# Revit family: Domotics-DomesticRanges-GEWISS-27COMBI_SYSTEM-IP55_4P+4P
name_source: partatom
category: Apparecchi elettrici
revit_build: Autodesk Revit 2016 (Build: 20161004_0715(x64)
units: mm (PartAtom-declared; Revit-internal decimal feet)

## family parameters
Condiviso = No
Host = Superficie
Mantenere orientamento annotazione = No
Numero OmniClass = 23.80.30.14.24
Punto di calcolo locali = No
Quota connettore circolare = Usa diametro
Taglio con vuoti quando caricato = Sì
Tipo di parte = Normale
Titolo OmniClass = Junction Boxes

## types (1)
- Domotics-DomesticRanges-GEWISS-27COMBI_SYSTEM-IP55_4P+4P
    Catalogue = DOMOTICS
    Catalogue Range = 27COMBI
    Colour = Grey RAL 7035
    Compartment pre-arrangement = 2
    Configuration = Module 4 x 2
    Description: = 8 gang
    Descrizione = VERT.8(2X4) GANG ENCLOSURE IP55
    Door colour: = Transparent
    Door type = With membrane
    EAN code = 8011564055407
    Electrocod = 0212
    Glow Wire Test = 650°C
    IDF = bff38524-b723-44e9-9b8f-3ff32b0260b1
    IDT = 3990d046-d57d-4ccd-aa40-94a36558d188
    IP degree = IP55
    Immagine tipo = gw27051.jpg
    Installation temperature = -25 +60 °C
    Insulation class = II
    Lid screws = Stainless steel
    Modello = GW27051
    No. SYSTEM modules = 8 gang
    No. knockout holes Ã˜23 = 10 on sides / 2 on the bottom
    Outer dim. LxHxD (mm) = 132x171x65
    Produttore = GEWISS S.p.A.
    Prospetto di default = 1219 mm
    SEO = Enclosure
    Shock resistance = IK07
    Standard; = EN 60670-1
    Technical sheet = https://www.gewiss.com
    Thermo-pressure with ball = 70
    Torque screws tightening = 0,8NM
    Type of knockout holes = Removable with tool
    URL = https://www.gewiss.com
    Version file RFA = 19.4

note: source unit labels omitted for Thermo-pressure with ball — the stored unit's dimension contradicts the parameter name (converter mislabeling)
